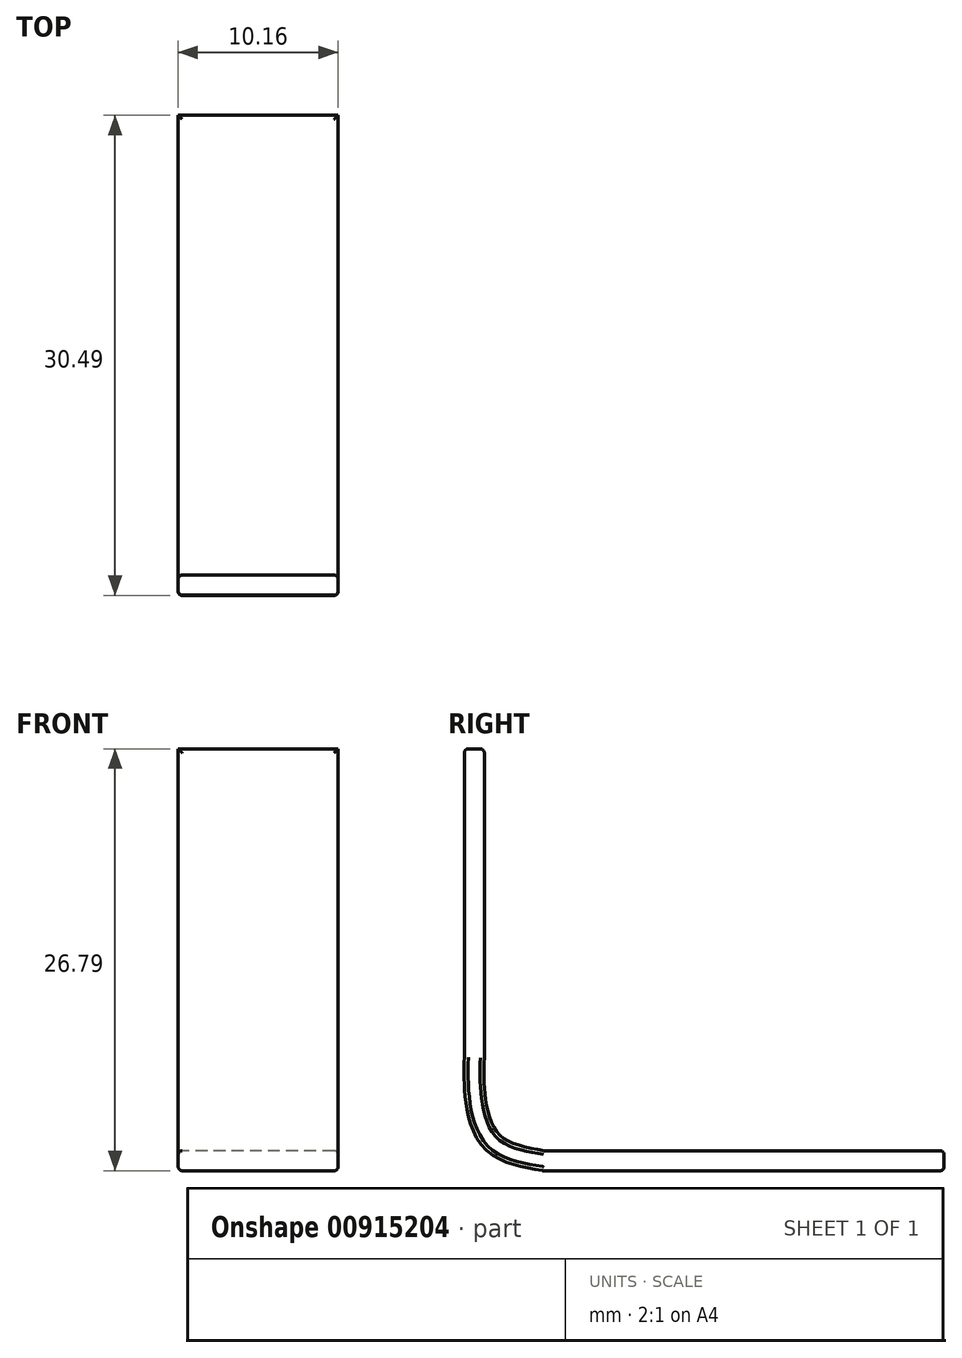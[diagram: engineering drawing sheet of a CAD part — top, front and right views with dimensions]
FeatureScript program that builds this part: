
annotation { "Feature Type Name" : "Feature", "Feature Type Description" : "" }
export const myFeature = defineFeature(function(context is Context, id is Id, definition is map)
    precondition{}
    {
        {
            var Q0;
            Q0=qCreatedBy(makeId("Front.planeOp"),FACE);
            var sketch = newSketch(context, id + "F0", { "sketchPlane" : qUnion([Q0])});
            skLineSegment(sketch, "E0.bottom", {"start": v(-5.1, 0.4) * mm, "end": v(5.05, 0.4) * mm});
            skLineSegment(sketch, "E0.top", {"start": v(-5.1, -0.87) * mm, "end": v(5.05, -0.87) * mm});
            skLineSegment(sketch, "E0.left", {"start": v(-5.1, 0.4) * mm, "end": v(-5.1, -0.87) * mm});
            skLineSegment(sketch, "E0.right", {"start": v(5.05, 0.4) * mm, "end": v(5.05, -0.87) * mm});
            skSolve(sketch);
        }
        {
            var Q0;
            Q0=qCreatedBy(makeId("Right.planeOp"),FACE);
            var sketch = newSketch(context, id + "F1", { "sketchPlane" : qUnion([Q0])});
            skLineSegment(sketch, "E1", {"start": v(0, 0) * mm, "end": v(-25.4, 0) * mm});
            skFitSpline(sketch, "E2", {"points": [v(-25.4, 0) * mm, v(-28.54, 1.14) * mm, v(-29.56, 4.04) * mm, v(-29.6, 6.3) * mm], "startDerivative": vector(-10.12, 1.69) * mm, "endDerivative": vector(0.22, 7.16) * mm});
            skLineSegment(sketch, "E3", {"start": v(-29.6, 6.3) * mm, "end": v(-29.6, 25.92) * mm});
            skSolve(sketch);
        }
        {
            var Q0;
            Q0=makeQuery(id+"F0.imprint","IMPRINT",FACE,{"disambiguationData":[TD([[makeQuery(id+"F0.imprint","IMPRINT",EDGE,{"derivedFrom":sQuery(id+"F0.wireOp",EDGE,"E0.bottom")}),-1.0]])]});
            var Q1;
            Q1=sQuery(id+"F1.wireOp",EDGE,"E1");
            var Q2;
            Q2=sQuery(id+"F1.wireOp",EDGE,"E2");
            var Q3;
            Q3=sQuery(id+"F1.wireOp",EDGE,"E3");
            sweep(context, id + "F2", {"profiles" : qUnion([Q0]), "path" : qUnion([Q1, Q2, Q3])});
        }
        {
            var Q0;
            Q0=makeQuery(id+"F2.opSweep","SWEPT_FACE",FACE,{"disambiguationData":[OSD([sQuery(id+"F0.wireOp",EDGE,"E0.bottom"),sQuery(id+"F1.wireOp",EDGE,"E3")])]});
            var Q1;
            Q1=makeQuery(id+"F2.opSweep","SWEPT_FACE",FACE,{"disambiguationData":[OSD([sQuery(id+"F0.wireOp",EDGE,"E0.bottom"),sQuery(id+"F1.wireOp",EDGE,"E2")])]});
            var Q2;
            Q2=makeQuery(id+"F2.opSweep","SWEPT_FACE",FACE,{"disambiguationData":[OSD([sQuery(id+"F0.wireOp",EDGE,"E0.bottom"),sQuery(id+"F1.wireOp",EDGE,"E1")])]});
            var Q3;
            Q3=makeQuery(id+"F2.opSweep","SWEPT_FACE",FACE,{"disambiguationData":[OSD([sQuery(id+"F0.wireOp",EDGE,"E0.top"),sQuery(id+"F1.wireOp",EDGE,"E1")])]});
            var Q4;
            Q4=makeQuery(id+"F2.opSweep","SWEPT_FACE",FACE,{"disambiguationData":[OSD([sQuery(id+"F0.wireOp",EDGE,"E0.top"),sQuery(id+"F1.wireOp",EDGE,"E2")])]});
            var Q5;
            Q5=makeQuery(id+"F2.opSweep","SWEPT_FACE",FACE,{"disambiguationData":[OSD([sQuery(id+"F0.wireOp",EDGE,"E0.top"),sQuery(id+"F1.wireOp",EDGE,"E3")])]});
            fillet(context, id + "F3", {"entities" : qUnion([Q0, Q1, Q2, Q3, Q4, Q5]), "tangentPropagation" : true, "radius" : 0.25 * mm, "defaultsChanged" : false, "vertexSettings" : [], "allowEdgeOverflow" : false});
        }
    });
